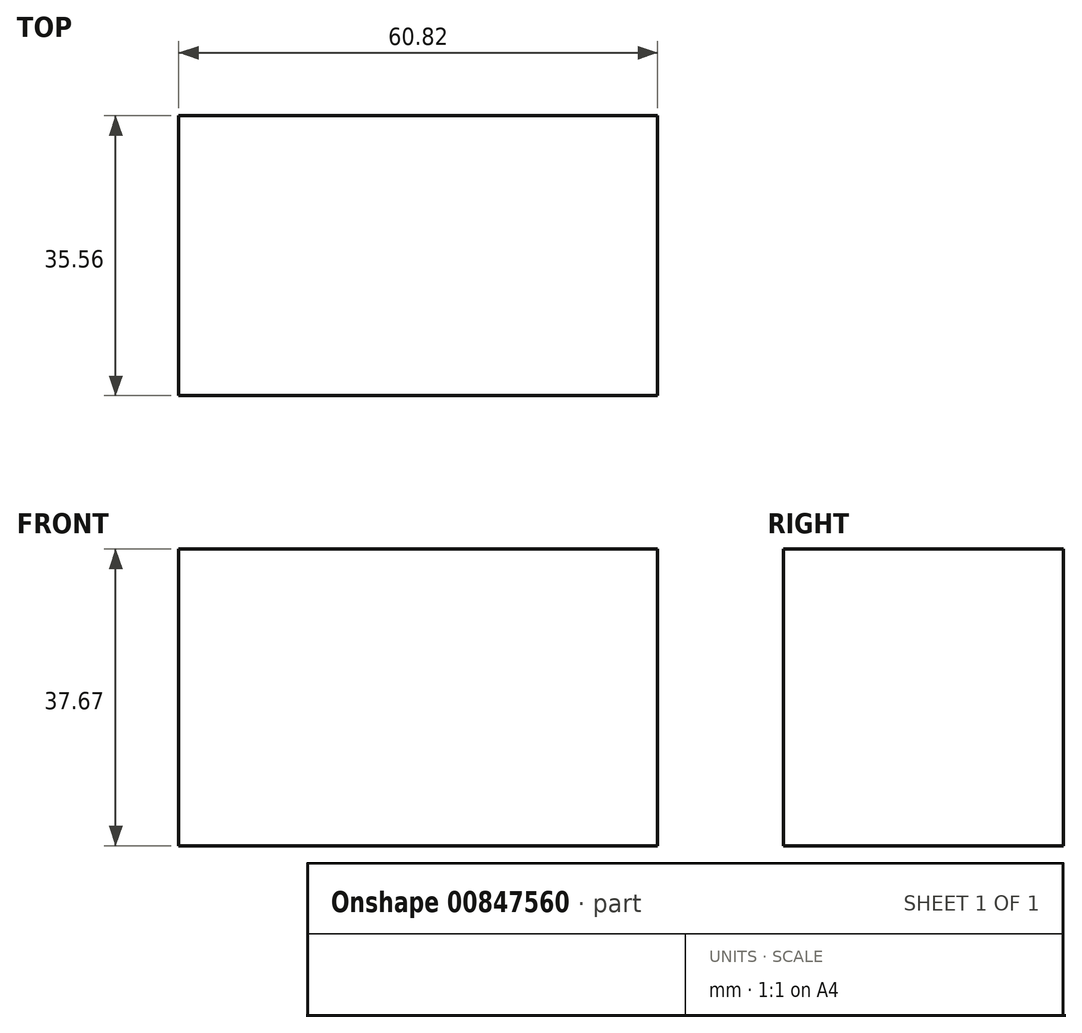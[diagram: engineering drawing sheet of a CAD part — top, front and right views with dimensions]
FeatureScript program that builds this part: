
annotation { "Feature Type Name" : "Feature", "Feature Type Description" : "" }
export const myFeature = defineFeature(function(context is Context, id is Id, definition is map)
    precondition{}
    {
        {
            var Q0;
            Q0=qCreatedBy(makeId("Front.planeOp"),FACE);
            var sketch = newSketch(context, id + "F0", { "sketchPlane" : qUnion([Q0])});
            skLineSegment(sketch, "E0.bottom", {"start": v(0, 0) * mm, "end": v(60.82, 0) * mm});
            skLineSegment(sketch, "E0.top", {"start": v(0, 37.67) * mm, "end": v(60.82, 37.67) * mm});
            skLineSegment(sketch, "E0.left", {"start": v(0, 0) * mm, "end": v(0, 37.67) * mm});
            skLineSegment(sketch, "E0.right", {"start": v(60.82, 0) * mm, "end": v(60.82, 37.67) * mm});
            skSolve(sketch);
        }
        {
            var Q0;
            Q0=makeQuery(id+"F0.imprint","IMPRINT",FACE,{"disambiguationData":[TD([[makeQuery(id+"F0.imprint","IMPRINT",EDGE,{"derivedFrom":sQuery(id+"F0.wireOp",EDGE,"E0.bottom")}),1.0]])]});
            extrude(context, id + "F1", {"entities" : qUnion([Q0]), "depth" : 35.56 * mm, "offsetDistance" : 25.4 * mm});
        }
    });
